# Revit family: 35-7310-60-OS
name_source: partatom
category: Luminarias
revit_build: Autodesk Revit 2017 (Build: 20160225_1515(x64)
units: mm (PartAtom-declared; Revit-internal decimal feet)

## family parameters
Anfitrión = Cara
Compartido = Sí
Corte con vacíos al cargar = No
Cota de conector redondo = Diámetro de uso
Número OmniClass = 23.80.70.00
Origen de luz = No
Punto de cálculo de habitación = No
Tipo de pieza = Normal
Título OmniClass = Lighting

## types (1)
- 35-7310-60-OS
    Acabado = Negro
    CRI = 90
    Carga aparente = 0 VA
    Catálogo = Technical
    CodigoGubimclass = 50.60.50.20
    CodigoOmniclass = 21-04 50 40
    CodigoUniclass2015 = EF_70_80
    CodigoUniformat2010 = D5040
    DescripcionGubimclass = Iluminación interior
    DescripcionOmniclass = Lighting
    DescripcionUniclass2015 = Lighting
    DescripcionUniformat2010 = Lighting
    EAN13 = 8435526868605
    Eficiencia energética = LED A++
    Elevación por defecto = 1000 mm  [stored 3.28084 ft]
    Etiqueta V/f = 220-240V/50-60Hz
    Fabricante = LEDS C4
    Familia = Atom Track 75
    FechaVersion = Julio 2020
    Ficha = http://files.leds-c4.com
    Fotometría = http://files.leds-c4.com
    Fuente de luz = 1xLED 24 2775.00 lm
    IMC = http://files.leds-c4.com
    IP = IP20
    IfcExportAs = IfcLightFixture
IfcLightFixture
    IfcExportType = NOTDEFINED
    Imagen web = http://files.leds-c4.com
    LDT = http://files.leds-c4.com
    Lumenes reales (lm) = 1567
    Material = Aluminio, Policarbonato, Policarbonato
    Peso neto (KG) = 0.64
    Pluma comercial = http://files.leds-c4.com
    Producto descatalogado = Catalogado ES
    Rayo de luz = ULTRA FLOOD
    Referencia = 35-7310-60-OS
    Temperatura color led (K) = Blanco cálido - 3000K
    Tender text (Castellano) = LEDS C4
Atom Track 75
35-7310-60-OS

Proyector de uso interior con iluminación orientable. 

Alto rendimiento lm/W real. Uso de lentes para un óptimo control lumínico y minimización del halo residual. Compacto y de alto rendimiento. Fuente de luz orientable. Material estructura: Aluminio, Policarbonato. Acabado estructura: Negro. Material difusor: Policarbonato. Garantía: 5 Años.

Peso neto del producto (Kg): 0.640
Anchura o diámetro del producto (mm): 75
Altura del producto (mm): 185

Clase 2. IP: IP20. LED. Nº de portalámparas o Leds: 1. Marca del LED: CREE. Marca del Driver: TRIDONIC. Potencia máxima de la fuente de luz: 24W. Temperatura de color: Blanco cálido - 3000K. Índice de reproducción cromática: 90. Steps Mac Adam: 2. Diámetro máximo de la bombilla que admite la luminaria: 50.000h L80B20. UGR:  14.7. Riesgo fotobiológico: RG1. % de Flickering: &lt;5%. Flujo real (lm): 1567. Flujo nominal (lm): 2775. Lm/W reales: 56. Rango de voltaje/frecuencia: 220-240/50-60Hz. Voltaje: 35. Equipo incluido: Si, electrónico. Potencia total: 28. Factor de potencia: 0.90.
    Tender text (English) = LEDS C4
Atom Track 75
35-7310-60-OS

Spotlight for indoor use. 

With adjustable lighting positioning. High performance effective lm/W. Lenses allow optimum control of illumination with minimal residual halo. Compact, high performance product. Adjustable light source. Structure material: Aluminium, Polycarbonate. Structure finish: Black. Diffuser material: Polycarbonate. Warranty: 5 Years.

Product net weight (Kg): 0.640
Product width or diameter (mm): 75
Product height (mm): 185

Class 2. IP: IP20. LED. No. of lampholders or LEDs: 1. LED brand: CREE. Driver brand: TRIDONIC. Maximum power of light source: 24W. Colour temperature: LED warm-white 3000K. Colour rendering index: 90. MacAdam Steps: 2. Maximum diameter of luminaire bulb: 50.000h L80B20. UGR:  14.7. Photobiological risk: RG1. % de Flickering: &lt;5%. Real flux (lm): 1567. Nominal flux (lm): 2775. Lm/Real W: 56. Voltage and frequency range: 220-240/50-60Hz. Voltage: 35. Gear included: Yes, electronic. Total power: 28. Power factor: 0.90.
    Tipo = Proyector
    Vatios (W) = 28
    Versión = v1

note: [stored X ft] marks values corroborated as IEEE doubles in the binary element streams (Revit-internal decimal feet)
